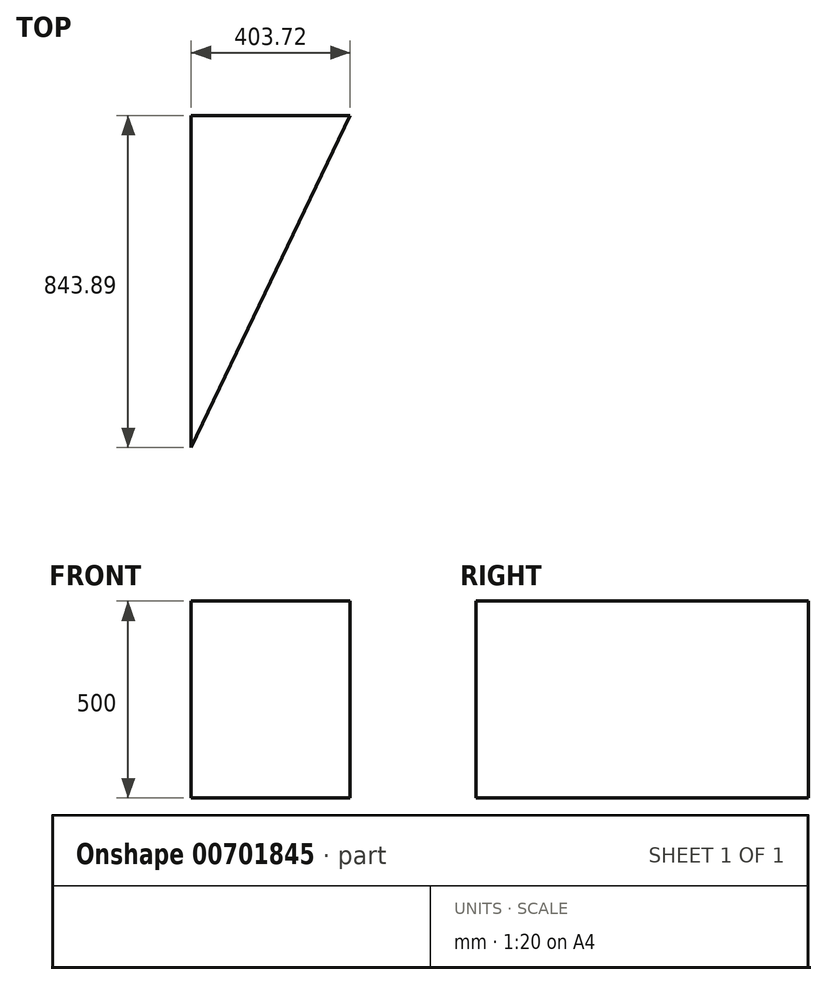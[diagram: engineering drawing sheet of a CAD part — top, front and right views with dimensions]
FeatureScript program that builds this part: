
annotation { "Feature Type Name" : "Feature", "Feature Type Description" : "" }
export const myFeature = defineFeature(function(context is Context, id is Id, definition is map)
    precondition{}
    {
        {
            var Q0;
            Q0=qCreatedBy(makeId("Top.planeOp"),FACE);
            var sketch = newSketch(context, id + "F0", { "sketchPlane" : qUnion([Q0])});
            skLineSegment(sketch, "E0", {"start": v(-304.8, 0) * mm, "end": v(-254, 444.5) * mm});
            skLineSegment(sketch, "E1", {"start": v(-254, 444.5) * mm, "end": v(254, 444.5) * mm});
            skLineSegment(sketch, "E2", {"start": v(254, 444.5) * mm, "end": v(304.8, 0) * mm});
            skLineSegment(sketch, "E3", {"start": v(304.8, 0) * mm, "end": v(-304.8, 0) * mm});
            skLineSegment(sketch, "E4", {"start": v(-254, 444.5) * mm, "end": v(0, 2667) * mm});
            skLineSegment(sketch, "E5", {"start": v(0, 2667) * mm, "end": v(254, 444.5) * mm});
            skSolve(sketch);
        }
        {
            var Q0;
            Q0=makeQuery(id+"F0.imprint","IMPRINT",FACE,{"disambiguationData":[TD([[makeQuery(id+"F0.imprint","IMPRINT",EDGE,{"derivedFrom":sQuery(id+"F0.wireOp",EDGE,"E1")}),1.0]])]});
            var sketch = newSketch(context, id + "F1", { "sketchPlane" : qUnion([Q0])});
            skSolve(sketch);
        }
        {
            var Q0;
            Q0=makeQuery(id+"F1.imprint","IMPRINT",FACE,{"disambiguationData":[TD([[makeQuery(id+"F1.imprint","IMPRINT",EDGE,{"derivedFrom":makeQuery(id+"F0.imprint","IMPRINT",EDGE,{"derivedFrom":sQuery(id+"F0.wireOp",EDGE,"E1")})}),1.0]])]});
            var sketch = newSketch(context, id + "F2", { "sketchPlane" : qUnion([Q0])});
            skLineSegment(sketch, "E6", {"start": v(-559.99, 1087.63) * mm, "end": v(-559.99, 1931.52) * mm});
            skLineSegment(sketch, "E7", {"start": v(-559.99, 1931.52) * mm, "end": v(-156.27, 1931.52) * mm});
            skLineSegment(sketch, "E8", {"start": v(-156.27, 1931.52) * mm, "end": v(-559.99, 1087.63) * mm});
            skSolve(sketch);
        }
        {
            var Q0;
            Q0 = qSketchRegion(id + "F2", true);
            extrude(context, id + "F3", {"entities" : qUnion([Q0]), "depth" : 500 * mm, "offsetDistance" : 25 * mm});
        }
    });
